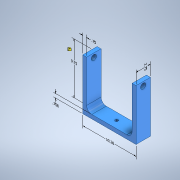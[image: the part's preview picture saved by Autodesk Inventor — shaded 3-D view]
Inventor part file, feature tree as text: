
AUTODESK INVENTOR PART (.ipt)
format: ipt  version: 2022.2 (Build 262287000, 287)  size: 296,448 bytes
history: native  units: in
note: dims shown in document units (in); Inventor stores cm internally (conversion verified against a paired STEP export)
features: other x6, sketch x5, extrude x4, thicken_offset x2, fillet x1, emboss x1
ambient origin geometry x8: Origin, YZ Plane, XZ Plane, XY Plane, X Axis, Y Axis, Z Axis, Center Point
bodies: Solid1 (feature_tree)
feature tree (19):
  other  "Annotations"
  extrude  "Extrusion1"  Depth=2.75in
  extrude  "Extrusion2"  Depth=0.75in
  extrude  "Extrusion3"  Depth=0.75in TaperAngle=0.0deg
  extrude  "Extrusion4"  TaperAngle=0.0deg  [1 undecoded]
  thicken_offset  "Thicken1"
  thicken_offset  "Thicken2"
  fillet  "Fillet2"  Radius=0.5in
  emboss  "Emboss1"
  sketch  "Sketch1"  dims[d0=10.2in d1=2.75in]
  sketch  "Sketch2"  dims[d2=0.75in d3=0.0in d4=0.75in]
  sketch  "Sketch3"  dims[d5=0.75in d6=9.0in d7=0.0in]
  sketch  "Sketch4"  dims[d8=1.0in d10=0.0in d11=0.0in d13=0.5in]
  sketch  "Sketch5"  dims[d14=0.0in d15=0.0in d16=0.005in d17=0.005in d18=0.005in d19=0.005in d22=1.0in d28=0.75in d39=0.1in d40=0.0in d23=0.1417in d24=0.75in d25=0.2606in d26=0.1203in d27=9.75in d30=0.2925in d31=0.3111in d32=0.75in d33=0.2465in d34=0.1211in d35=2.75in d36=0.0895in d37=0.24in d38=10.2in]
  other  "Linear Dimension 1"
  other  "Linear Dimension 2"
  other  "Linear Dimension 3"
  other  "Linear Dimension 4"
  other  "Linear Dimension 5"
note: 1 required parameter value undecoded (feature->parameter linkage not recoverable at this tier; creation-order binding heuristic only, values carry confidence <= 0.55)
